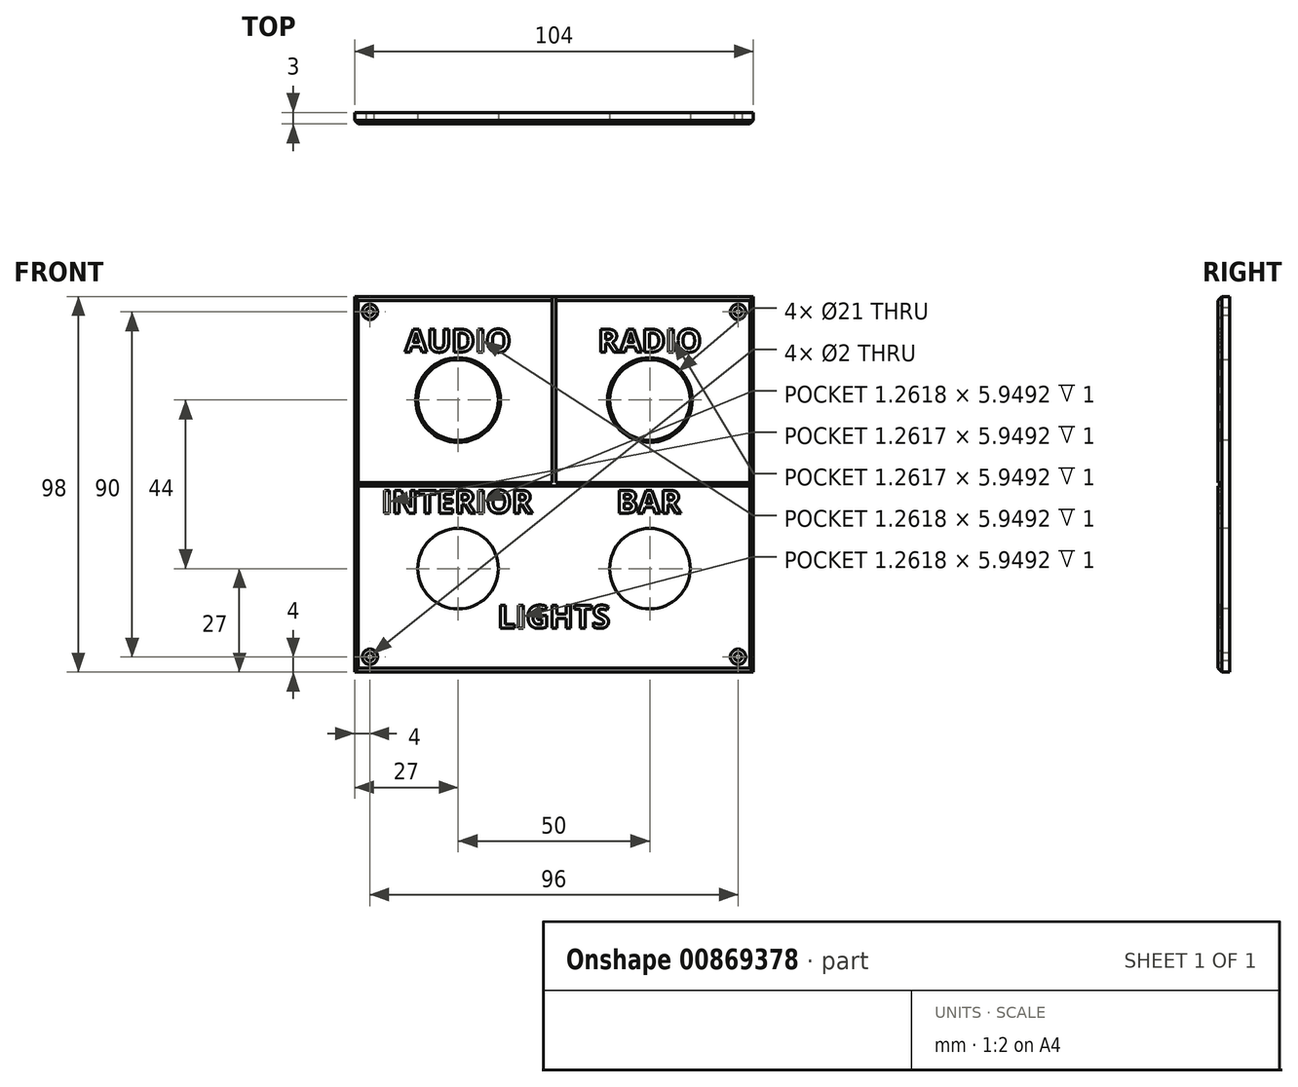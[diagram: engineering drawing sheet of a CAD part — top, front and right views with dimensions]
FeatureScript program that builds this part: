
annotation { "Feature Type Name" : "Feature", "Feature Type Description" : "" }
export const myFeature = defineFeature(function(context is Context, id is Id, definition is map)
    precondition{}
    {
        {
            var Q0;
            Q0=qCreatedBy(makeId("Front.planeOp"),FACE);
            var sketch = newSketch(context, id + "F0", { "sketchPlane" : qUnion([Q0])});
            skLineSegment(sketch, "E0.bottom", {"start": v(52, 49) * mm, "end": v(-52, 49) * mm});
            skLineSegment(sketch, "E0.top", {"start": v(52, -49) * mm, "end": v(-52, -49) * mm});
            skLineSegment(sketch, "E0.left", {"start": v(52, 49) * mm, "end": v(52, -49) * mm});
            skLineSegment(sketch, "E0.right", {"start": v(-52, 49) * mm, "end": v(-52, -49) * mm});
            skPoint(sketch, "E0.middle", {"position": v(0, 0) * mm});
            skCircle(sketch, "E1", {"center": v(-25, 22) * mm, "radius": 10.5 * mm});
            skCircle(sketch, "E2", {"center": v(25, 22) * mm, "radius": 10.5 * mm});
            skCircle(sketch, "E3", {"center": v(25, -22) * mm, "radius": 10.5 * mm});
            skCircle(sketch, "E4", {"center": v(-25, -22) * mm, "radius": 10.5 * mm});
            skLineSegment(sketch, "E5.bottom", {"start": v(25, 22) * mm, "end": v(-25, 22) * mm, "construction": true});
            skLineSegment(sketch, "E5.top", {"start": v(25, -22) * mm, "end": v(-25, -22) * mm, "construction": true});
            skLineSegment(sketch, "E5.left", {"start": v(25, 22) * mm, "end": v(25, -22) * mm, "construction": true});
            skLineSegment(sketch, "E5.right", {"start": v(-25, 22) * mm, "end": v(-25, -22) * mm, "construction": true});
            skCircle(sketch, "E6", {"center": v(-25, 22) * mm, "radius": 11.5 * mm, "construction": true});
            skCircle(sketch, "E7", {"center": v(25, 22) * mm, "radius": 11.5 * mm, "construction": true});
            skCircle(sketch, "E8", {"center": v(25, -22) * mm, "radius": 11.5 * mm, "construction": true});
            skCircle(sketch, "E9", {"center": v(-25, -22) * mm, "radius": 11.5 * mm, "construction": true});
            skCircle(sketch, "E10", {"center": v(-25, 22) * mm, "radius": 15 * mm, "construction": true});
            skCircle(sketch, "E11", {"center": v(-25, -22) * mm, "radius": 15 * mm, "construction": true});
            skCircle(sketch, "E12", {"center": v(25, 22) * mm, "radius": 15 * mm, "construction": true});
            skCircle(sketch, "E13", {"center": v(25, -22) * mm, "radius": 15 * mm, "construction": true});
            skPoint(sketch, "E14", {"position": v(-48, 45) * mm});
            skPoint(sketch, "E15", {"position": v(48, 45) * mm});
            skPoint(sketch, "E16", {"position": v(48, -45) * mm});
            skPoint(sketch, "E17", {"position": v(-48, -45) * mm});
            skLineSegment(sketch, "E18.bottom", {"start": v(-48, 45) * mm, "end": v(48, 45) * mm, "construction": true});
            skLineSegment(sketch, "E18.top", {"start": v(-48, -45) * mm, "end": v(48, -45) * mm, "construction": true});
            skLineSegment(sketch, "E18.left", {"start": v(-48, 45) * mm, "end": v(-48, -45) * mm, "construction": true});
            skLineSegment(sketch, "E18.right", {"start": v(48, 45) * mm, "end": v(48, -45) * mm, "construction": true});
            skCircle(sketch, "E19", {"center": v(0, -22) * mm, "radius": 10.5 * mm, "construction": true});
            skSolve(sketch);
        }
        {
            var Q0;
            Q0=makeQuery(id+"F0.imprint","IMPRINT",FACE,{"disambiguationData":[TD([[makeQuery(id+"F0.imprint","IMPRINT",EDGE,{"derivedFrom":sQuery(id+"F0.wireOp",EDGE,"E0.bottom")}),1.0]])]});
            extrude(context, id + "F1", {"entities" : qUnion([Q0]), "oppositeDirection" : true, "depth" : 3 * mm, "offsetDistance" : 25 * mm});
        }
        {
            var Q0;
            Q0=makeQuery(id+"F1.opExtrude","CAP_EDGE",EDGE,{"disambiguationData":[OSD([sQuery(id+"F0.wireOp",EDGE,"E0.bottom")])],"isStart":true});
            var Q1;
            Q1=makeQuery(id+"F1.opExtrude","CAP_EDGE",EDGE,{"disambiguationData":[OSD([sQuery(id+"F0.wireOp",EDGE,"E0.right")])],"isStart":true});
            var Q2;
            Q2=makeQuery(id+"F1.opExtrude","CAP_EDGE",EDGE,{"disambiguationData":[OSD([sQuery(id+"F0.wireOp",EDGE,"E0.left")])],"isStart":true});
            var Q3;
            Q3=makeQuery(id+"F1.opExtrude","CAP_EDGE",EDGE,{"disambiguationData":[OSD([sQuery(id+"F0.wireOp",EDGE,"E0.top")])],"isStart":true});
            chamfer(context, id + "F2", {"entities" : qUnion([Q0, Q1, Q2, Q3]), "width" : 1 * mm, "tangentPropagation" : true});
        }
        {
            var Q0;
            Q0=sQuery(id+"F0.wireOp",VERTEX,"E14");
            var Q1;
            Q1=sQuery(id+"F0.wireOp",VERTEX,"E15");
            var Q2;
            Q2=sQuery(id+"F0.wireOp",VERTEX,"E16");
            var Q3;
            Q3=sQuery(id+"F0.wireOp",VERTEX,"E17");
            var Q4;
            Q4=makeQuery(id+"F1.opExtrude","SWEPT_BODY",BODY,{"disambiguationData":[OSD([sQuery(id+"F0.wireOp",EDGE,"E0.bottom"),sQuery(id+"F0.wireOp",EDGE,"E0.top"),sQuery(id+"F0.wireOp",EDGE,"E0.left"),sQuery(id+"F0.wireOp",EDGE,"E0.right"),sQuery(id+"F0.wireOp",EDGE,"E1"),sQuery(id+"F0.wireOp",EDGE,"E2"),sQuery(id+"F0.wireOp",EDGE,"E3"),sQuery(id+"F0.wireOp",EDGE,"E4")])]});
            hole(context, id + "F3", {"style" : HoleStyle.C_SINK, "endStyle" : HoleEndStyle.THROUGH, "holeDiameter" : 2 * mm, "cSinkDiameter" : 4 * mm, "cSinkAngle" : 85 * degree, "majorDiameter" : 5 * mm, "isTappedThrough" : true, "tappedDepth" : 12 * mm, "tapClearance" : 3, "locations" : qUnion([Q0, Q1, Q2, Q3]), "scope" : qUnion([Q4])});
        }
        {
            var Q0;
            Q0=makeQuery(id+"F1.opExtrude","CAP_FACE",FACE,{"disambiguationData":[OSD([sQuery(id+"F0.wireOp",EDGE,"E0.bottom"),sQuery(id+"F0.wireOp",EDGE,"E0.top"),sQuery(id+"F0.wireOp",EDGE,"E0.left"),sQuery(id+"F0.wireOp",EDGE,"E0.right"),sQuery(id+"F0.wireOp",EDGE,"E1"),sQuery(id+"F0.wireOp",EDGE,"E2"),sQuery(id+"F0.wireOp",EDGE,"E3"),sQuery(id+"F0.wireOp",EDGE,"E4")])],"isStart":true});
            var sketch = newSketch(context, id + "F4", { "sketchPlane" : qUnion([Q0])});
            skText(sketch, "E20", { "text": "AUDIO", "fontName": "OpenSans-Bold.ttf"});
            skText(sketch, "E21", { "text": "RADIO", "fontName": "OpenSans-Bold.ttf"});
            skPoint(sketch, "E22", {"position": v(-25, 41.5) * mm});
            skPoint(sketch, "E23", {"position": v(25, 41.5) * mm});
            skPoint(sketch, "E24", {"position": v(-25, 22) * mm});
            skPoint(sketch, "E25", {"position": v(25, 22) * mm});
            skText(sketch, "E26", { "text": "INTERIOR", "fontName": "OpenSans-Bold.ttf"});
            skText(sketch, "E27", { "text": "BAR", "fontName": "OpenSans-Bold.ttf"});
            skPoint(sketch, "E28", {"position": v(-25, -22) * mm});
            skPoint(sketch, "E29", {"position": v(25, -22) * mm});
            skText(sketch, "E30", { "text": "LIGHTS", "fontName": "OpenSans-Bold.ttf"});
            skLineSegment(sketch, "E31.0", {"start": v(-52, 49) * mm, "end": v(52, 49) * mm, "construction": true});
            skLineSegment(sketch, "E32.0", {"start": v(-52, -49) * mm, "end": v(-52, 49) * mm, "construction": true});
            skLineSegment(sketch, "E33.0", {"start": v(52, 49) * mm, "end": v(52, -49) * mm, "construction": true});
            skLineSegment(sketch, "E34.0", {"start": v(52, -49) * mm, "end": v(-52, -49) * mm, "construction": true});
            skLineSegment(sketch, "E35", {"start": v(0, 49) * mm, "end": v(0, 0) * mm, "construction": true});
            skLineSegment(sketch, "E36", {"start": v(0, 0) * mm, "end": v(-52, 0) * mm, "construction": true});
            skLineSegment(sketch, "E37", {"start": v(0, 0) * mm, "end": v(52, 0) * mm, "construction": true});
            skLineSegment(sketch, "E38", {"start": v(-0.5, 49) * mm, "end": v(-0.5, 0.5) * mm});
            skLineSegment(sketch, "E39", {"start": v(-0.5, 0.5) * mm, "end": v(-52, 0.5) * mm});
            skLineSegment(sketch, "E40", {"start": v(0.5, 49) * mm, "end": v(0.5, 0.5) * mm});
            skLineSegment(sketch, "E41", {"start": v(0.5, 0.5) * mm, "end": v(52, 0.5) * mm});
            skLineSegment(sketch, "E42", {"start": v(52, -0.5) * mm, "end": v(-52, -0.5) * mm});
            skLineSegment(sketch, "E43", {"start": v(-52, -0.5) * mm, "end": v(-52, 0.5) * mm});
            skLineSegment(sketch, "E44", {"start": v(52, -0.5) * mm, "end": v(52, 0.5) * mm});
            skLineSegment(sketch, "E45", {"start": v(-0.5, 49) * mm, "end": v(0.5, 49) * mm});
            const initialGuessF4  = {"E20": [-0.03883, 0.0345, 1, 0, 0.006], "E21": [0.01148, 0.0345, 1, 0, 0.006], "E26": [-0.04498, -0.0075, 1, 0, 0.006], "E27": [0.0163, -0.0075, 1, 0, 0.006], "E30": [-0.01475, -0.0375, 1, 0, 0.006]};
            skSetInitialGuess(sketch, initialGuessF4);
            skSolve(sketch);
        }
        {
            var Q0;
            Q0=qSketchRegion(id+"F4",true);
            extrude(context, id + "F5", {"entities" : qUnion([Q0]), "operationType" : NewBodyOperationType.REMOVE, "oppositeDirection" : true, "depth" : 1 * mm, "offsetDistance" : 25 * mm});
        }
        {
            var Q0;
            Q0=makeQuery(id+"F1.opExtrude","CAP_EDGE",EDGE,{"disambiguationData":[OSD([sQuery(id+"F0.wireOp",EDGE,"E1")])],"isStart":true});
            var Q1;
            Q1=makeQuery(id+"F1.opExtrude","CAP_EDGE",EDGE,{"disambiguationData":[OSD([sQuery(id+"F0.wireOp",EDGE,"E2")])],"isStart":true});
            var Q2;
            Q2=makeQuery(id+"F1.opExtrude","CAP_EDGE",EDGE,{"disambiguationData":[OSD([sQuery(id+"F0.wireOp",EDGE,"E19")])],"isStart":true});
            chamfer(context, id + "F6", {"entities" : qUnion([Q0, Q1, Q2]), "width" : .55 * mm, "tangentPropagation" : true});
        }
    });
